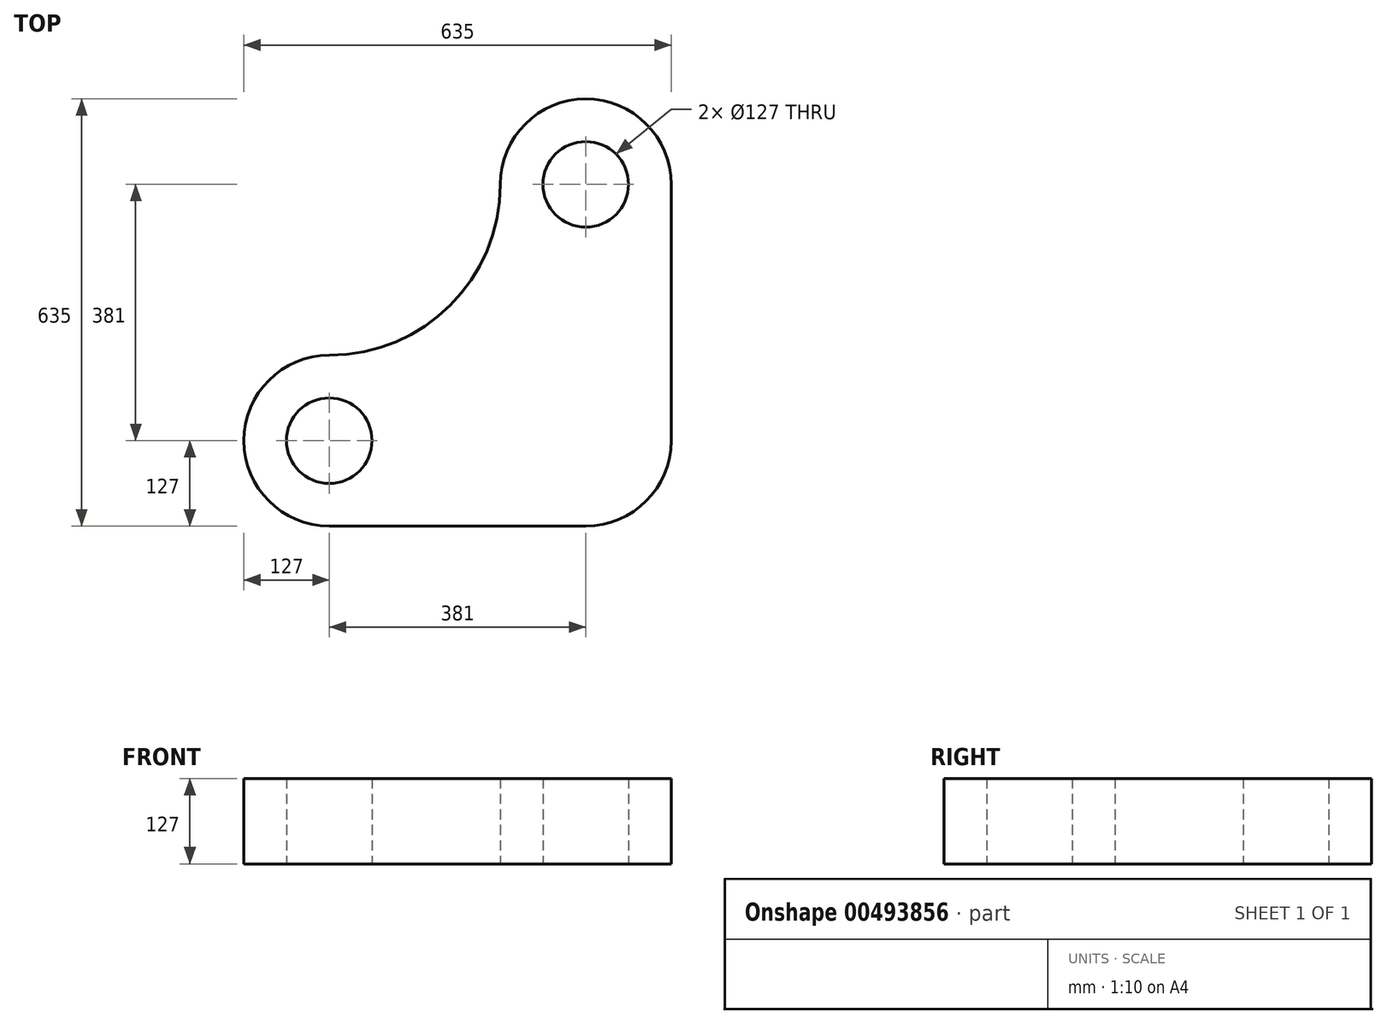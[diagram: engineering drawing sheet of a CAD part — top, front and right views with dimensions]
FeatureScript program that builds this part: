
annotation { "Feature Type Name" : "Feature", "Feature Type Description" : "" }
export const myFeature = defineFeature(function(context is Context, id is Id, definition is map)
    precondition{}
    {
        {
            var Q0;
            Q0=qCreatedBy(makeId("Top.planeOp"),FACE);
            var sketch = newSketch(context, id + "F0", { "sketchPlane" : qUnion([Q0])});
            skArc(sketch, "E0", {"start": v(127, 381) * mm, "mid": v(0, 508) * mm, "end": v(-127, 381) * mm});
            skArc(sketch, "E1", {"start": v(-381, 127) * mm, "mid": v(-201.4, 201.4) * mm, "end": v(-127, 381) * mm});
            skArc(sketch, "E2", {"start": v(-381, 127) * mm, "mid": v(-508, 0) * mm, "end": v(-381, -127) * mm});
            skLineSegment(sketch, "E3", {"start": v(-381, -127) * mm, "end": v(0, -127) * mm});
            skArc(sketch, "E4", {"start": v(0, -127) * mm, "mid": v(89.8, -89.8) * mm, "end": v(127, 0) * mm});
            skLineSegment(sketch, "E5", {"start": v(127, 0) * mm, "end": v(127, 381) * mm});
            skCircle(sketch, "E6", {"center": v(-381, 0) * mm, "radius": 63.5 * mm});
            skCircle(sketch, "E7", {"center": v(0, 381) * mm, "radius": 63.5 * mm});
            skSolve(sketch);
        }
        {
            var Q0;
            Q0 = qSketchRegion(id + "F0", true);
            extrude(context, id + "F1", {"entities" : qUnion([Q0]), "depth" : 127 * mm});
        }
    });
